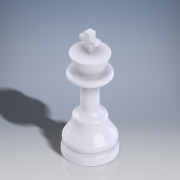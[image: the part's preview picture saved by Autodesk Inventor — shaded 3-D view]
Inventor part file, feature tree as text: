
AUTODESK INVENTOR PART (.ipt)
format: ipt  version: 2018 (Build 220112000, 112)  size: 370,688 bytes
history: native  units: in
note: dims shown in document units (in); Inventor stores cm internally (conversion verified against a paired STEP export)
features: fillet x14, extrude x10, sketch x10, chamfer x3, draft x1
ambient origin geometry x8: Origin, YZ Plane, XZ Plane, XY Plane, X Axis, Y Axis, Z Axis, Center Point
bodies: Solid1 (feature_tree)
feature tree (38):
  extrude  "Extrusion1"  Depth=0.2in TaperAngle=0.0deg
  fillet  "Fillet1"  Radius=0.1in
  extrude  "Extrusion2"  Depth=0.1in
  fillet  "Fillet2"  Radius=0.025in
  fillet  "Fillet3"  Radius=0.096in
  chamfer  "Chamfer1"  Distance=0.0625in
  extrude  "Extrusion3"  Depth=0.125in
  chamfer  "Chamfer2"  Distance=0.2835in
  fillet  "Fillet4"  Radius=0.375in
  fillet  "Fillet5"  Radius=0.0625in
  fillet  "Fillet6"  Radius=0.33in
  extrude  "Extrusion4"  Depth=0.1875in
  fillet  "Fillet7"  Radius=0.125in
  fillet  "Fillet8"  Radius=0.1875in
  extrude  "Extrusion5"  Depth=0.475in
  fillet  "Fillet9"  Radius=0.375in
  extrude  "Extrusion6"  Depth=0.148in
  fillet  "Fillet10"  Radius=0.4375in
  fillet  "Fillet11"  Radius=0.125in
  extrude  "Extrusion7"  Depth=0.125in TaperAngle=0.0deg
  draft  "FaceDraft1"
  extrude  "Extrusion8"  Depth=0.0225in
  extrude  "Extrusion9"  Depth=0.0225in
  extrude  "Extrusion10"  Depth=0.0225in
  fillet  "Fillet12"  Radius=0.015in
  fillet  "Fillet13"  [1 undecoded]
  fillet  "Fillet14"  [1 undecoded]
  chamfer  "Chamfer3"  [1 undecoded]
  sketch  "Sketch1"  dims[d0=1.0in d1=0.2in d2=0.0in d3=0.1in]
  sketch  "Sketch2"  dims[d4=0.2in d5=0.0in d6=0.1in d7=0.025in]
  sketch  "Sketch3"  dims[d8=0.0625in d9=0.125in d10=0.3917in d11=0.096in d12=0.0in d13=0.0625in d14=0.125in d15=0.3779in]
  sketch  "Sketch4"  dims[d16=0.025in d17=0.125in]
  sketch  "Sketch5"  dims[d18=0.125in d19=0.2835in d20=0.0in d21=0.375in d22=0.0625in d23=0.33in]
  sketch  "Sketch6"  dims[d24=0.75in d25=0.0in d26=0.1875in d27=0.125in d28=0.0in d29=0.1875in]
  sketch  "Sketch7"  dims[d30=0.0625in d31=0.475in d32=0.375in d33=0.0in]
  sketch  "Sketch8"  dims[d34=-0.1374in d35=0.148in d36=0.4375in d37=0.0in d38=0.125in]
  sketch  "Sketch9"  dims[d39=0.1in d40=0.125in d41=0.0in]
  sketch  "Sketch10"  dims[d42=0.125in d43=0.0in d44=0.0225in d45=0.0225in d46=0.0225in d47=0.015in d48=0.125in d49=45.0deg]
note: 3 required parameter values undecoded (feature->parameter linkage not recoverable at this tier; creation-order binding heuristic only, values carry confidence <= 0.55)
